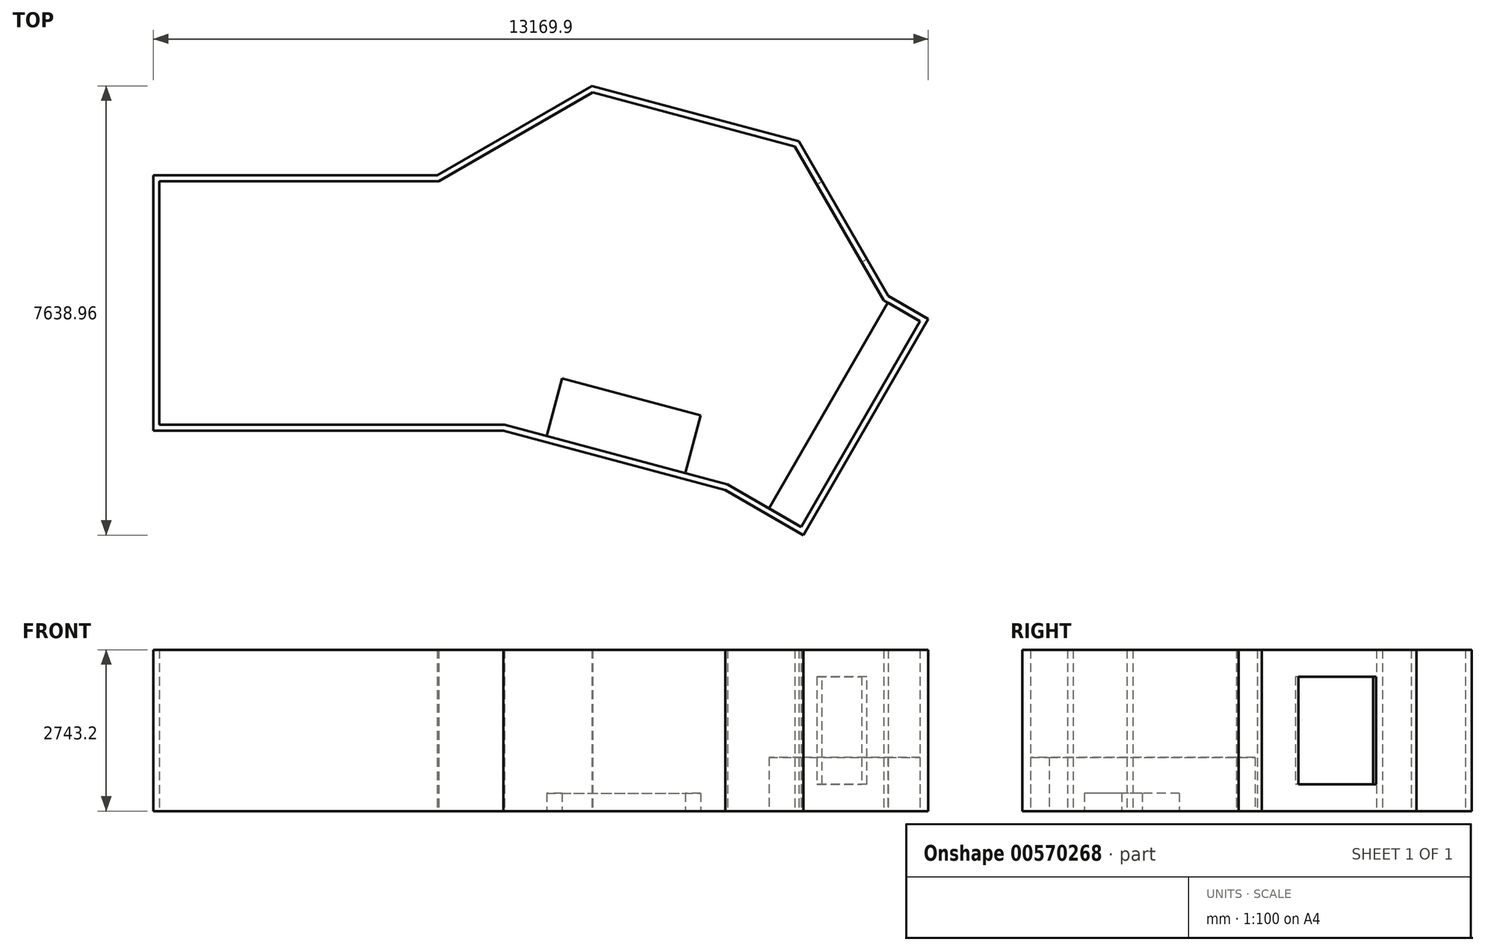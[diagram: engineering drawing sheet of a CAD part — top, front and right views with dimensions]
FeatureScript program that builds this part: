
annotation { "Feature Type Name" : "Feature", "Feature Type Description" : "" }
export const myFeature = defineFeature(function(context is Context, id is Id, definition is map)
    precondition{}
    {
        {
            var Q0;
            Q0=qCreatedBy(makeId("Top.planeOp"),FACE);
            var sketch = newSketch(context, id + "F0", { "sketchPlane" : qUnion([Q0])});
            skLineSegment(sketch, "E0", {"start": v(0, 0) * mm, "end": v(4749.8, 0) * mm});
            skLineSegment(sketch, "E1", {"start": v(0, 0) * mm, "end": v(0, -4140.2) * mm});
            skLineSegment(sketch, "E2", {"start": v(0, -4140.2) * mm, "end": v(5862.84, -4140.2) * mm});
            skLineSegment(sketch, "E3", {"start": v(4749.8, 0) * mm, "end": v(7367.45, 1511.3) * mm});
            skLineSegment(sketch, "E4", {"start": v(7367.45, 1511.3) * mm, "end": v(10802.28, 590.94) * mm});
            skLineSegment(sketch, "E5", {"start": v(10802.28, 590.94) * mm, "end": v(12313.58, -2026.7) * mm});
            skLineSegment(sketch, "E6", {"start": v(12313.58, -2026.7) * mm, "end": v(12929.5, -2382.3) * mm});
            skLineSegment(sketch, "E7", {"start": v(12929.5, -2382.3) * mm, "end": v(10910.2, -5879.84) * mm});
            skLineSegment(sketch, "E8", {"start": v(7571.2, -4597.95) * mm, "end": v(9658.73, -5157.3) * mm});
            skLineSegment(sketch, "E9", {"start": v(10910.2, -5879.84) * mm, "end": v(9658.73, -5157.3) * mm});
            skLineSegment(sketch, "E10", {"start": v(7571.2, -4597.95) * mm, "end": v(5862.84, -4140.2) * mm});
            skLineSegment(sketch, "E11.0", {"start": v(12387.96, -1952.33) * mm, "end": v(13068.29, -2345.12) * mm});
            skLineSegment(sketch, "E11.1", {"start": v(10869.23, 678.19) * mm, "end": v(12387.96, -1952.33) * mm});
            skLineSegment(sketch, "E11.2", {"start": v(7353.1, 1620.33) * mm, "end": v(10869.23, 678.19) * mm});
            skLineSegment(sketch, "E11.3", {"start": v(4722.58, 101.6) * mm, "end": v(7353.1, 1620.33) * mm});
            skLineSegment(sketch, "E11.4", {"start": v(-101.6, 101.6) * mm, "end": v(4722.58, 101.6) * mm});
            skLineSegment(sketch, "E11.5", {"start": v(13068.29, -2345.12) * mm, "end": v(10947.39, -6018.63) * mm});
            skLineSegment(sketch, "E11.6", {"start": v(10947.39, -6018.63) * mm, "end": v(9619.52, -5251.98) * mm});
            skLineSegment(sketch, "E11.7", {"start": v(7544.9, -4696.1) * mm, "end": v(9619.52, -5251.98) * mm});
            skLineSegment(sketch, "E11.8", {"start": v(7544.9, -4696.1) * mm, "end": v(5849.47, -4241.8) * mm});
            skLineSegment(sketch, "E11.9", {"start": v(-101.6, -4241.8) * mm, "end": v(5849.47, -4241.8) * mm});
            skLineSegment(sketch, "E11.10", {"start": v(-101.6, 101.6) * mm, "end": v(-101.6, -4241.8) * mm});
            skSolve(sketch);
        }
        {
            var Q0;
            Q0 = qSketchRegion(id + "F0", true);
            extrude(context, id + "F1", {"entities" : qUnion([Q0]), "depth" : 2743.2 * mm, "offsetDistance" : 25.4 * mm});
        }
        {
            var Q0;
            Q0=makeQuery(id+"F1.opExtrude","CAP_FACE",FACE,{"disambiguationData":[OSD([sQuery(id+"F0.wireOp",EDGE,"E0"),sQuery(id+"F0.wireOp",EDGE,"E1"),sQuery(id+"F0.wireOp",EDGE,"E2"),sQuery(id+"F0.wireOp",EDGE,"E3"),sQuery(id+"F0.wireOp",EDGE,"E4"),sQuery(id+"F0.wireOp",EDGE,"E5"),sQuery(id+"F0.wireOp",EDGE,"E6"),sQuery(id+"F0.wireOp",EDGE,"E7"),sQuery(id+"F0.wireOp",EDGE,"E8"),sQuery(id+"F0.wireOp",EDGE,"E9"),sQuery(id+"F0.wireOp",EDGE,"E10"),sQuery(id+"F0.wireOp",EDGE,"E11.0"),sQuery(id+"F0.wireOp",EDGE,"E11.1"),sQuery(id+"F0.wireOp",EDGE,"E11.2"),sQuery(id+"F0.wireOp",EDGE,"E11.3"),sQuery(id+"F0.wireOp",EDGE,"E11.4"),sQuery(id+"F0.wireOp",EDGE,"E11.5"),sQuery(id+"F0.wireOp",EDGE,"E11.6"),sQuery(id+"F0.wireOp",EDGE,"E11.7"),sQuery(id+"F0.wireOp",EDGE,"E11.8"),sQuery(id+"F0.wireOp",EDGE,"E11.9"),sQuery(id+"F0.wireOp",EDGE,"E11.10")])],"isStart":true});
            var sketch = newSketch(context, id + "F2", { "sketchPlane" : qUnion([Q0])});
            skLineSegment(sketch, "E12", {"start": v(12929.5, 2382.3) * mm, "end": v(10910.2, 5879.84) * mm});
            skLineSegment(sketch, "E13", {"start": v(10910.2, 5879.84) * mm, "end": v(10360.27, 5562.34) * mm});
            skLineSegment(sketch, "E14", {"start": v(10360.27, 5562.34) * mm, "end": v(12379.57, 2064.8) * mm});
            skLineSegment(sketch, "E15", {"start": v(12379.57, 2064.8) * mm, "end": v(12929.5, 2382.3) * mm});
            skSolve(sketch);
        }
        {
            var Q0;
            Q0 = qSketchRegion(id + "F2", true);
            extrude(context, id + "F3", {"entities" : qUnion([Q0]), "oppositeDirection" : true, "depth" : 914.4 * mm, "offsetDistance" : 25.4 * mm});
        }
        {
            var Q0;
            Q0=makeQuery(id+"F1.opExtrude","SWEPT_FACE",FACE,{"disambiguationData":[OSD([sQuery(id+"F0.wireOp",EDGE,"E5")])]});
            var sketch = newSketch(context, id + "F4", { "sketchPlane" : qUnion([Q0])});
            skLineSegment(sketch, "E16", {"start": v(6400.67, 2743.2) * mm, "end": v(6400.67, 0) * mm, "construction": true});
            skLineSegment(sketch, "E17.bottom", {"start": v(5638.67, 2286) * mm, "end": v(7162.67, 2286) * mm});
            skLineSegment(sketch, "E17.top", {"start": v(5638.67, 457.2) * mm, "end": v(7162.67, 457.2) * mm});
            skLineSegment(sketch, "E17.left", {"start": v(5638.67, 2286) * mm, "end": v(5638.67, 457.2) * mm});
            skLineSegment(sketch, "E17.right", {"start": v(7162.67, 2286) * mm, "end": v(7162.67, 457.2) * mm});
            skSolve(sketch);
        }
        {
            var Q0;
            Q0 = qSketchRegion(id + "F4", true);
            extrude(context, id + "F5", {"entities" : qUnion([Q0]), "operationType" : NewBodyOperationType.REMOVE, "endBound" : BoundingType.THROUGH_ALL, "oppositeDirection" : true, "depth" : 25.4 * mm, "offsetDistance" : 25.4 * mm});
        }
        {
            var Q0;
            Q0=makeQuery(id+"F1.opExtrude","CAP_FACE",FACE,{"disambiguationData":[OSD([sQuery(id+"F0.wireOp",EDGE,"E0"),sQuery(id+"F0.wireOp",EDGE,"E1"),sQuery(id+"F0.wireOp",EDGE,"E2"),sQuery(id+"F0.wireOp",EDGE,"E3"),sQuery(id+"F0.wireOp",EDGE,"E4"),sQuery(id+"F0.wireOp",EDGE,"E5"),sQuery(id+"F0.wireOp",EDGE,"E6"),sQuery(id+"F0.wireOp",EDGE,"E7"),sQuery(id+"F0.wireOp",EDGE,"E8"),sQuery(id+"F0.wireOp",EDGE,"E9"),sQuery(id+"F0.wireOp",EDGE,"E10"),sQuery(id+"F0.wireOp",EDGE,"E11.0"),sQuery(id+"F0.wireOp",EDGE,"E11.1"),sQuery(id+"F0.wireOp",EDGE,"E11.2"),sQuery(id+"F0.wireOp",EDGE,"E11.3"),sQuery(id+"F0.wireOp",EDGE,"E11.4"),sQuery(id+"F0.wireOp",EDGE,"E11.5"),sQuery(id+"F0.wireOp",EDGE,"E11.6"),sQuery(id+"F0.wireOp",EDGE,"E11.7"),sQuery(id+"F0.wireOp",EDGE,"E11.8"),sQuery(id+"F0.wireOp",EDGE,"E11.9"),sQuery(id+"F0.wireOp",EDGE,"E11.10")])],"isStart":true});
            var sketch = newSketch(context, id + "F6", { "sketchPlane" : qUnion([Q0])});
            skLineSegment(sketch, "E18", {"start": v(6846.1, 3351.82) * mm, "end": v(6583.13, 4333.2) * mm});
            skLineSegment(sketch, "E19", {"start": v(9201.4, 3982.92) * mm, "end": v(8938.45, 4964.3) * mm});
            skLineSegment(sketch, "E20", {"start": v(8938.45, 4964.3) * mm, "end": v(6583.13, 4333.2) * mm});
            skLineSegment(sketch, "E21", {"start": v(6846.1, 3351.82) * mm, "end": v(9201.4, 3982.92) * mm});
            skSolve(sketch);
        }
        {
            var Q0;
            Q0 = qSketchRegion(id + "F6", true);
            extrude(context, id + "F7", {"entities" : qUnion([Q0]), "oppositeDirection" : true, "depth" : 304.8 * mm, "offsetDistance" : 25.4 * mm});
        }
    });
